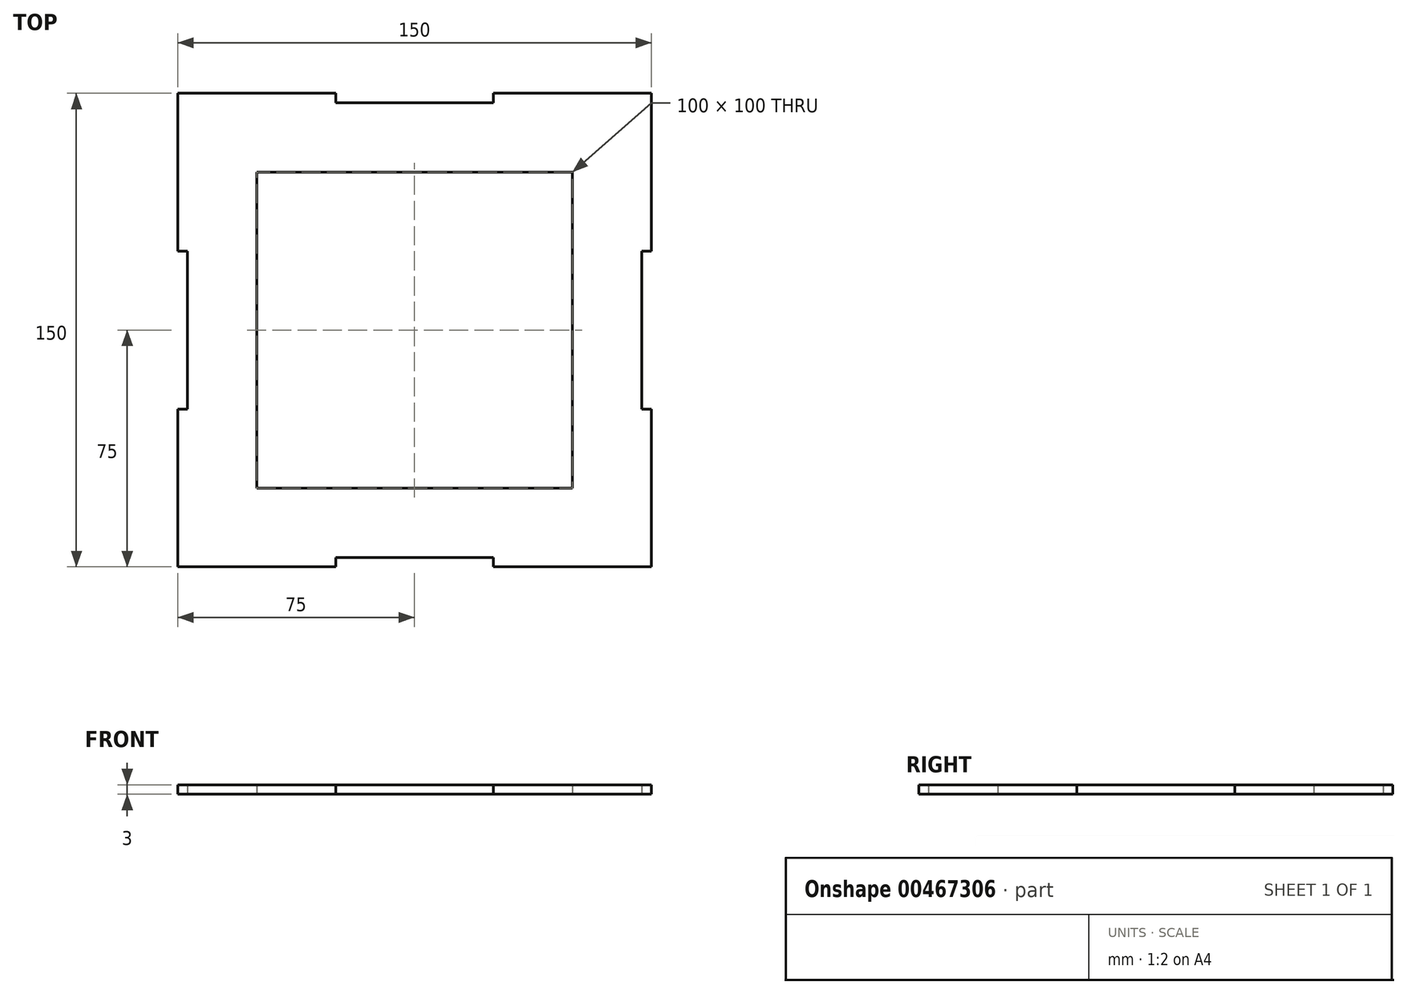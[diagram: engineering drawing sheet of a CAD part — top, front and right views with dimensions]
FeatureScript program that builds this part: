
annotation { "Feature Type Name" : "Feature", "Feature Type Description" : "" }
export const myFeature = defineFeature(function(context is Context, id is Id, definition is map)
    precondition{}
    {
        {
            var Q0;
            Q0=qCreatedBy(makeId("Top.planeOp"),FACE);
            var sketch = newSketch(context, id + "F0", { "sketchPlane" : qUnion([Q0])});
            skLineSegment(sketch, "E0.bottom", {"start": v(75, 75) * mm, "end": v(25, 75) * mm});
            skLineSegment(sketch, "E0.top", {"start": v(75, -75) * mm, "end": v(25, -75) * mm});
            skLineSegment(sketch, "E0.left", {"start": v(75, 75) * mm, "end": v(75, 25) * mm});
            skLineSegment(sketch, "E0.right", {"start": v(-75, 75) * mm, "end": v(-75, 25) * mm});
            skPoint(sketch, "E0.middle", {"position": v(0, 0) * mm});
            skLineSegment(sketch, "E1", {"start": v(-75, 25) * mm, "end": v(-72, 25) * mm});
            skLineSegment(sketch, "E2", {"start": v(-72, 25) * mm, "end": v(-72, -25) * mm});
            skLineSegment(sketch, "E3", {"start": v(-72, -25) * mm, "end": v(-75, -25) * mm});
            skLineSegment(sketch, "E4.trimOffspring", {"start": v(-75, -25) * mm, "end": v(-75, -75) * mm});
            skLineSegment(sketch, "E5", {"start": v(-75, 75) * mm, "end": v(-25, 75) * mm});
            skLineSegment(sketch, "E6", {"start": v(-25, 75) * mm, "end": v(-25, 72) * mm});
            skLineSegment(sketch, "E7", {"start": v(-25, 72) * mm, "end": v(25, 72) * mm});
            skLineSegment(sketch, "E8", {"start": v(25, 72) * mm, "end": v(25, 75) * mm});
            skLineSegment(sketch, "E9.trimOffspring", {"start": v(-25, 75) * mm, "end": v(-75, 75) * mm});
            skLineSegment(sketch, "E10", {"start": v(75, 25) * mm, "end": v(72, 25) * mm});
            skLineSegment(sketch, "E11", {"start": v(72, 25) * mm, "end": v(72, -25) * mm});
            skLineSegment(sketch, "E12", {"start": v(72, -25) * mm, "end": v(75, -25) * mm});
            skLineSegment(sketch, "E13.trimOffspring", {"start": v(75, -25) * mm, "end": v(75, -75) * mm});
            skLineSegment(sketch, "E14", {"start": v(-75, -75) * mm, "end": v(-25, -75) * mm});
            skLineSegment(sketch, "E15", {"start": v(-25, -75) * mm, "end": v(-25, -72) * mm});
            skLineSegment(sketch, "E16", {"start": v(-25, -72) * mm, "end": v(25, -72) * mm});
            skLineSegment(sketch, "E17", {"start": v(25, -72) * mm, "end": v(25, -75) * mm});
            skLineSegment(sketch, "E18.trimOffspring", {"start": v(-25, -75) * mm, "end": v(-75, -75) * mm});
            skLineSegment(sketch, "E19.bottom", {"start": v(50, 50) * mm, "end": v(-50, 50) * mm});
            skLineSegment(sketch, "E19.top", {"start": v(50, -50) * mm, "end": v(-50, -50) * mm});
            skLineSegment(sketch, "E19.left", {"start": v(50, 50) * mm, "end": v(50, -50) * mm});
            skLineSegment(sketch, "E19.right", {"start": v(-50, 50) * mm, "end": v(-50, -50) * mm});
            skSolve(sketch);
        }
        {
            var Q0;
            Q0=makeQuery(id+"F0.imprint","IMPRINT",FACE,{"disambiguationData":[TD([[makeQuery(id+"F0.imprint","IMPRINT",EDGE,{"derivedFrom":sQuery(id+"F0.wireOp",EDGE,"E0.bottom")}),1.0]])]});
            extrude(context, id + "F1", {"entities" : qUnion([Q0]), "depth" : 3 * mm});
        }
    });
